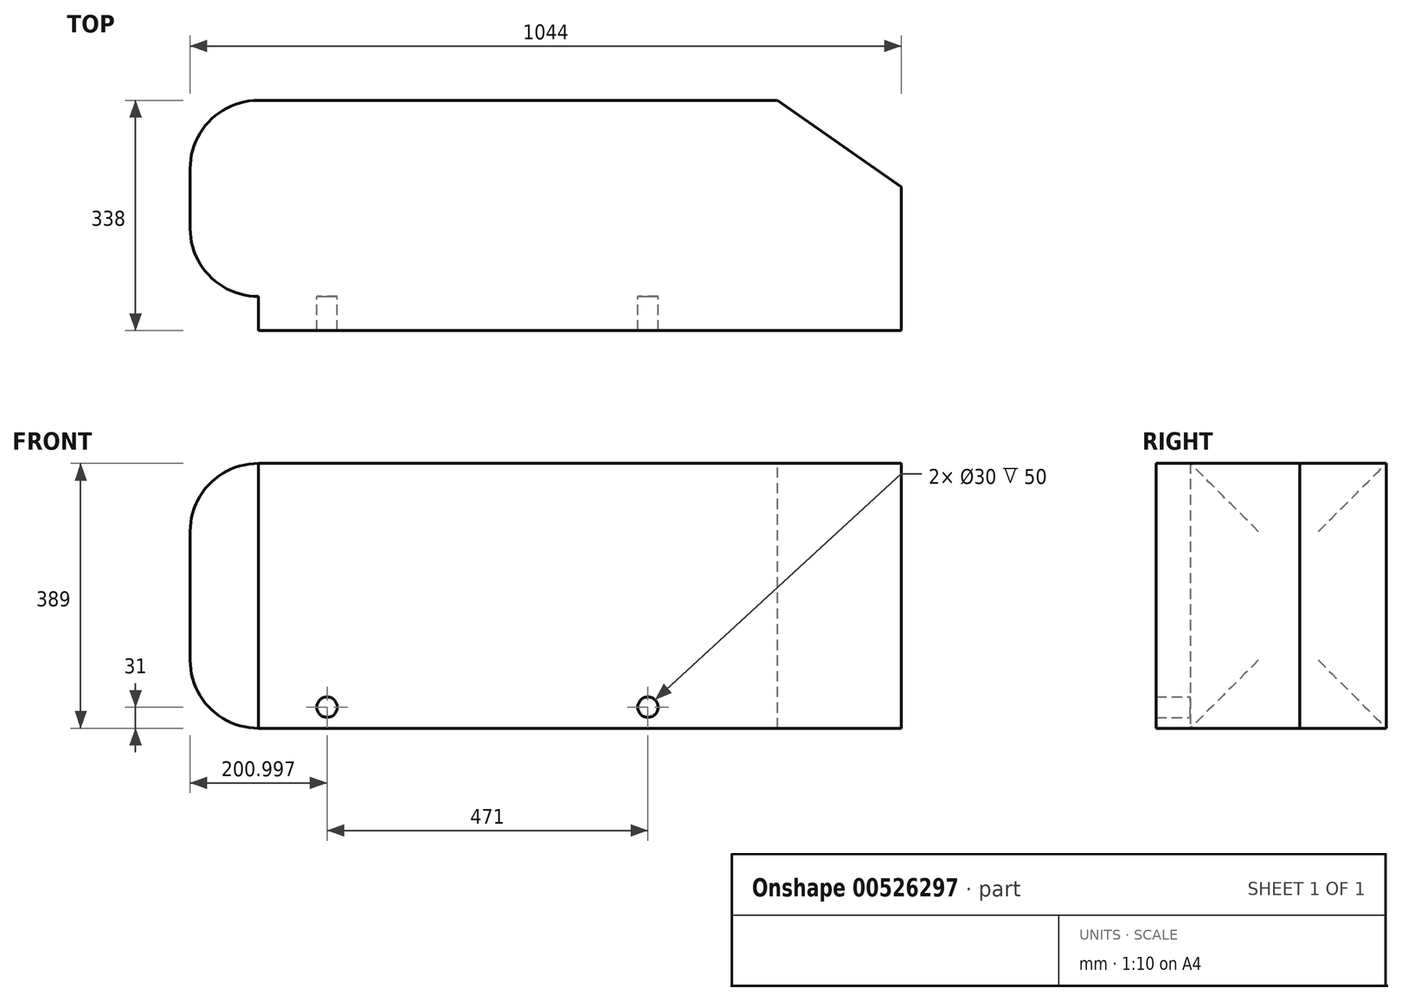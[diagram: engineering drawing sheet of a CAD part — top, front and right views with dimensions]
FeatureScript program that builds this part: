
annotation { "Feature Type Name" : "Feature", "Feature Type Description" : "" }
export const myFeature = defineFeature(function(context is Context, id is Id, definition is map)
    precondition{}
    {
        {
            assignVariable(context, id + "F0", {"name" : "piede", "anyValue" : 50});
        }
        {
            var Q0;
            Q0=qCreatedBy(makeId("Front.planeOp"),FACE);
            var sketch = newSketch(context, id + "F1", { "sketchPlane" : qUnion([Q0])});
            skLineSegment(sketch, "E0.bottom", {"start": v(-515.63, 194.5) * mm, "end": v(528.37, 194.5) * mm});
            skLineSegment(sketch, "E0.top", {"start": v(-515.63, -194.5) * mm, "end": v(528.37, -194.5) * mm});
            skLineSegment(sketch, "E0.left", {"start": v(-515.63, 194.5) * mm, "end": v(-515.63, -194.5) * mm});
            skLineSegment(sketch, "E0.right", {"start": v(528.37, 194.5) * mm, "end": v(528.37, -194.5) * mm});
            skSolve(sketch);
        }
        {
            var Q0;
            Q0=makeQuery(id+"F1.imprint","IMPRINT",FACE,{"disambiguationData":[TD([[makeQuery(id+"F1.imprint","IMPRINT",EDGE,{"derivedFrom":sQuery(id+"F1.wireOp",EDGE,"E0.bottom")}),-1.0]])]});
            extrude(context, id + "F2", {"entities" : qUnion([Q0]), "oppositeDirection" : true, "depth" : 288 * mm, "offsetDistance" : 25 * mm});
        }
        {
            var Q0;
            Q0=makeQuery(id+"F2.opExtrude","SWEPT_FACE",FACE,{"disambiguationData":[OSD([sQuery(id+"F1.wireOp",EDGE,"E0.left")])]});
            fillet(context, id + "F3", {"entities" : qUnion([Q0]), "radius" : 100 * mm, "tangentPropagation" : true, "allowEdgeOverflow" : false});
        }
        {
            var Q0;
            Q0=makeQuery(id+"F2.opExtrude","SWEPT_FACE",FACE,{"disambiguationData":[OSD([sQuery(id+"F1.wireOp",EDGE,"E0.bottom")])]});
            var sketch = newSketch(context, id + "F4", { "sketchPlane" : qUnion([Q0])});
            skLineSegment(sketch, "E1", {"start": v(346.52, 288) * mm, "end": v(528.37, 160.67) * mm});
            skLineSegment(sketch, "E2", {"start": v(528.37, 160.67) * mm, "end": v(528.37, 288) * mm});
            skLineSegment(sketch, "E3", {"start": v(528.37, 288) * mm, "end": v(346.52, 288) * mm});
            skSolve(sketch);
        }
        {
            var Q0;
            Q0 = qSketchRegion(id + "F4", true);
            extrude(context, id + "F5", {"entities" : qUnion([Q0]), "operationType" : NewBodyOperationType.REMOVE, "endBound" : BoundingType.THROUGH_ALL, "oppositeDirection" : true, "depth" : 25 * mm, "offsetDistance" : 25 * mm});
        }
        {
            var Q0;
            Q0=makeQuery(id+"F2.opExtrude","CAP_FACE",FACE,{"disambiguationData":[OSD([sQuery(id+"F1.wireOp",EDGE,"E0.bottom"),sQuery(id+"F1.wireOp",EDGE,"E0.top"),sQuery(id+"F1.wireOp",EDGE,"E0.left"),sQuery(id+"F1.wireOp",EDGE,"E0.right")])],"isStart":true});
            var sketch = newSketch(context, id + "F6", { "sketchPlane" : qUnion([Q0])});
            skCircle(sketch, "E4", {"center": v(-314.63, 163.5) * mm, "radius": 15 * mm});
            skCircle(sketch, "E5", {"center": v(156.37, 163.5) * mm, "radius": 15 * mm});
            skLineSegment(sketch, "E6", {"start": v(-415.63, 0) * mm, "end": v(528.37, 0) * mm, "construction": true});
            skCircle(sketch, "E7.MirrorC", {"center": v(-314.63, -163.5) * mm, "radius": 15 * mm});
            skCircle(sketch, "E8.MirrorC", {"center": v(156.37, -163.5) * mm, "radius": 15 * mm});
            skSolve(sketch);
        }
        {
            var Q0;
            Q0=makeQuery(id+"F6.imprint","IMPRINT",FACE,{"disambiguationData":[TD([[makeQuery(id+"F6.imprint","IMPRINT",EDGE,{"derivedFrom":sQuery(id+"F6.wireOp",EDGE,"E4")}),1.0]])]});
            var Q1;
            Q1=makeQuery(id+"F6.imprint","IMPRINT",FACE,{"disambiguationData":[TD([[makeQuery(id+"F6.imprint","IMPRINT",EDGE,{"derivedFrom":sQuery(id+"F6.wireOp",EDGE,"E5")}),1.0]])]});
            var Q2;
            Q2=makeQuery(id+"F6.imprint","IMPRINT",FACE,{"disambiguationData":[TD([[makeQuery(id+"F6.imprint","IMPRINT",EDGE,{"derivedFrom":sQuery(id+"F6.wireOp",EDGE,"E8.MirrorC")}),-1.0]])]});
            var Q3;
            Q3=makeQuery(id+"F6.imprint","IMPRINT",FACE,{"disambiguationData":[TD([[makeQuery(id+"F6.imprint","IMPRINT",EDGE,{"derivedFrom":sQuery(id+"F6.wireOp",EDGE,"E7.MirrorC")}),-1.0]])]});
            extrude(context, id + "F7", {"entities" : qUnion([Q0, Q1, Q2, Q3]), "operationType" : NewBodyOperationType.ADD, "depth" : (getVariable(context, 'piede')) * mm, "offsetDistance" : 25 * mm});
        }
        {
            var Q0;
            Q0=makeQuery(id+"F2.opExtrude","SWEPT_BODY",BODY,{"disambiguationData":[OSD([sQuery(id+"F1.wireOp",EDGE,"E0.bottom"),sQuery(id+"F1.wireOp",EDGE,"E0.top"),sQuery(id+"F1.wireOp",EDGE,"E0.left"),sQuery(id+"F1.wireOp",EDGE,"E0.right")])]});
            transform(context, id + "F8", {"entities" : qUnion([Q0]), "transformType" : TransformType.TRANSLATION_3D, "dx" : 0 * mm, "dy" : 50 * mm, "dz" : 0 * mm, "makeCopy" : false});
        }
    });
